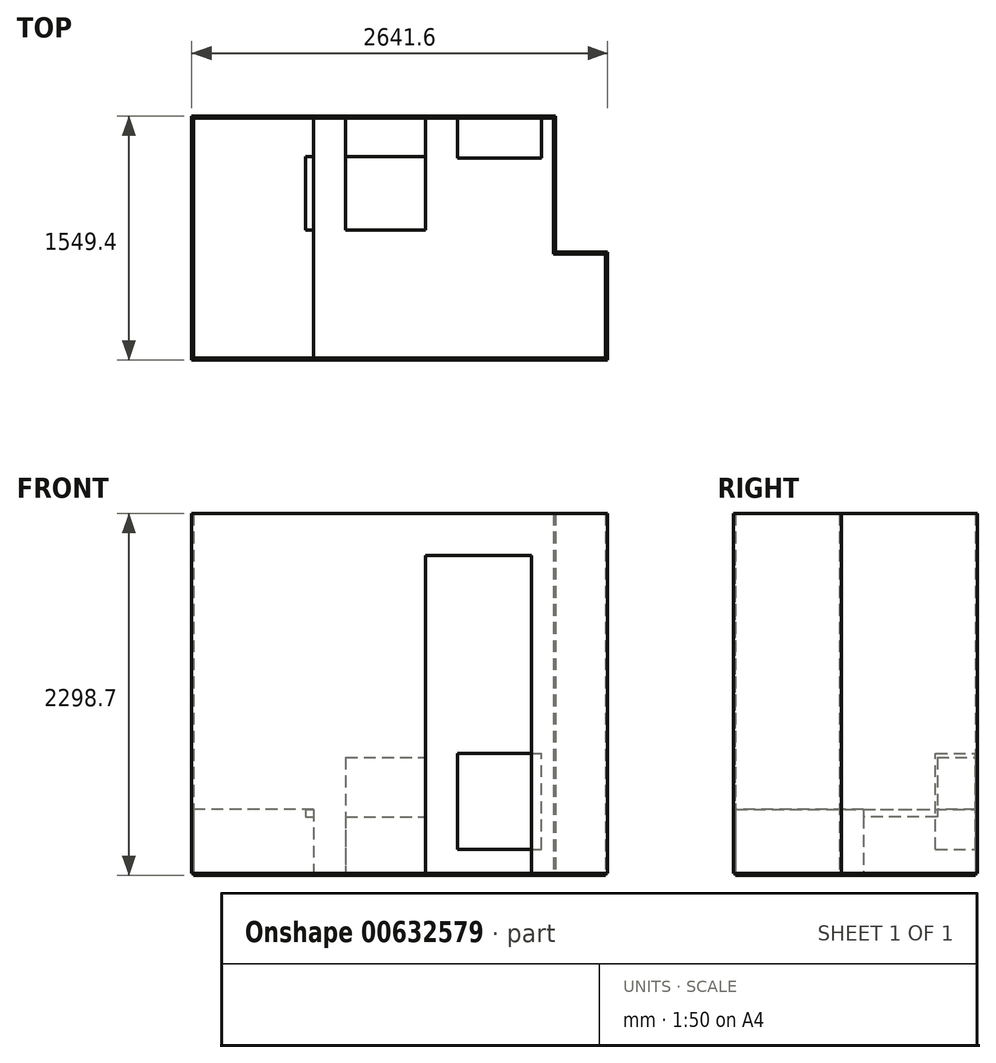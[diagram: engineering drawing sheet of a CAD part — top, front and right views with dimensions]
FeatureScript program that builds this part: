
annotation { "Feature Type Name" : "Feature", "Feature Type Description" : "" }
export const myFeature = defineFeature(function(context is Context, id is Id, definition is map)
    precondition{}
    {
        {
            var Q0;
            Q0=qCreatedBy(makeId("Top.planeOp"),FACE);
            var sketch = newSketch(context, id + "F0", { "sketchPlane" : qUnion([Q0])});
            skLineSegment(sketch, "E0.bottom", {"start": v(1143, -762) * mm, "end": v(-1143, -762) * mm});
            skLineSegment(sketch, "E0.top", {"start": v(1143, 762) * mm, "end": v(-1143, 762) * mm});
            skLineSegment(sketch, "E0.left", {"start": v(1143, -101.6) * mm, "end": v(1143, 762) * mm});
            skLineSegment(sketch, "E0.right", {"start": v(-1143, -762) * mm, "end": v(-1143, 762) * mm});
            skPoint(sketch, "E0.middle", {"position": v(0, 0) * mm});
            skLineSegment(sketch, "E1.bottom", {"start": v(1143, -762) * mm, "end": v(1473.2, -762) * mm});
            skLineSegment(sketch, "E1.top", {"start": v(1143, -101.6) * mm, "end": v(1473.2, -101.6) * mm});
            skLineSegment(sketch, "E1.right", {"start": v(1473.2, -762) * mm, "end": v(1473.2, -101.6) * mm});
            skSolve(sketch);
        }
        {
            var Q0;
            Q0=makeQuery(id+"F0.imprint","IMPRINT",FACE,{"disambiguationData":[TD([[makeQuery(id+"F0.imprint","IMPRINT",EDGE,{"derivedFrom":sQuery(id+"F0.wireOp",EDGE,"E0.bottom")}),-1.0]])]});
            extrude(context, id + "F1", {"entities" : qUnion([Q0]), "oppositeDirection" : true, "depth" : 12.7 * mm, "offsetDistance" : 25.4 * mm});
        }
        {
            var Q0;
            Q0=makeQuery(id+"F1.opExtrude","CAP_FACE",FACE,{"disambiguationData":[OSD([sQuery(id+"F0.wireOp",EDGE,"E0.bottom"),sQuery(id+"F0.wireOp",EDGE,"E0.top"),sQuery(id+"F0.wireOp",EDGE,"E0.left"),sQuery(id+"F0.wireOp",EDGE,"E0.right"),sQuery(id+"F0.wireOp",EDGE,"E1.bottom"),sQuery(id+"F0.wireOp",EDGE,"E1.top"),sQuery(id+"F0.wireOp",EDGE,"E1.right")])],"isStart":true});
            var sketch = newSketch(context, id + "F2", { "sketchPlane" : qUnion([Q0])});
            skLineSegment(sketch, "E2.0", {"start": v(1485.9, -774.7) * mm, "end": v(1485.9, -88.9) * mm});
            skLineSegment(sketch, "E2.1", {"start": v(1155.7, -88.9) * mm, "end": v(1155.7, 774.7) * mm});
            skLineSegment(sketch, "E2.2", {"start": v(1155.7, 774.7) * mm, "end": v(-1155.7, 774.7) * mm});
            skLineSegment(sketch, "E2.3", {"start": v(1485.9, -88.9) * mm, "end": v(1155.7, -88.9) * mm});
            skLineSegment(sketch, "E2.4", {"start": v(-1155.7, 774.7) * mm, "end": v(-1155.7, -774.7) * mm});
            skLineSegment(sketch, "E2.5", {"start": v(-1155.7, -774.7) * mm, "end": v(1485.9, -774.7) * mm});
            skSolve(sketch);
        }
        {
            var Q0;
            Q0=makeQuery(id+"F2.imprint","IMPRINT",FACE,{"disambiguationData":[TD([[makeQuery(id+"F2.imprint","IMPRINT",EDGE,{"derivedFrom":sQuery(id+"F2.wireOp",EDGE,"E2.0")}),1.0]])]});
            extrude(context, id + "F3", {"entities" : qUnion([Q0]), "depth" : 2286 * mm, "offsetDistance" : 25.4 * mm});
        }
        {
            var Q0;
            Q0=makeQuery(id+"F3.opExtrude","SWEPT_FACE",FACE,{"disambiguationData":[OSD([sQuery(id+"F2.wireOp",EDGE,"E2.5")])]});
            var sketch = newSketch(context, id + "F4", { "sketchPlane" : qUnion([Q0])});
            skLineSegment(sketch, "E3.bottom", {"start": v(330.2, 0) * mm, "end": v(1003.3, 0) * mm});
            skLineSegment(sketch, "E3.left", {"start": v(330.2, 0) * mm, "end": v(330.2, 2019.3) * mm});
            skLineSegment(sketch, "E3.right", {"start": v(1003.3, 0) * mm, "end": v(1003.3, 2019.3) * mm});
            skLineSegment(sketch, "E4", {"start": v(330.2, 2019.3) * mm, "end": v(1003.3, 2019.3) * mm});
            skPoint(sketch, "E3.top.end.orphan", {"position": v(1003.3, 2286) * mm});
            skPoint(sketch, "E3.top.start.orphan", {"position": v(330.2, 2286) * mm});
            skSolve(sketch);
        }
        {
            var Q0;
            Q0 = qSketchRegion(id + "F4", true);
            extrude(context, id + "F5", {"entities" : qUnion([Q0]), "operationType" : NewBodyOperationType.REMOVE, "oppositeDirection" : true, "depth" : 25.4 * mm, "offsetDistance" : 25.4 * mm});
        }
        {
            var Q0;
            Q0=makeQuery(id+"F1.opExtrude","CAP_FACE",FACE,{"disambiguationData":[OSD([sQuery(id+"F0.wireOp",EDGE,"E0.bottom"),sQuery(id+"F0.wireOp",EDGE,"E0.top"),sQuery(id+"F0.wireOp",EDGE,"E0.left"),sQuery(id+"F0.wireOp",EDGE,"E0.right"),sQuery(id+"F0.wireOp",EDGE,"E1.bottom"),sQuery(id+"F0.wireOp",EDGE,"E1.top"),sQuery(id+"F0.wireOp",EDGE,"E1.right")])],"isStart":true});
            var sketch = newSketch(context, id + "F6", { "sketchPlane" : qUnion([Q0])});
            skLineSegment(sketch, "E5.bottom", {"start": v(-1143, 762) * mm, "end": v(-381, 762) * mm});
            skLineSegment(sketch, "E5.top", {"start": v(-1143, -762) * mm, "end": v(-381, -762) * mm});
            skLineSegment(sketch, "E5.left", {"start": v(-1143, 762) * mm, "end": v(-1143, -762) * mm});
            skLineSegment(sketch, "E5.right", {"start": v(-381, 762) * mm, "end": v(-381, -762) * mm});
            skSolve(sketch);
        }
        {
            var Q0;
            Q0=makeQuery(id+"F3.opExtrude","SWEPT_FACE",FACE,{"disambiguationData":[OSD([sQuery(id+"F0.wireOp",EDGE,"E0.top")])]});
            var sketch = newSketch(context, id + "F7", { "sketchPlane" : qUnion([Q0])});
            skSolve(sketch);
        }
        {
            var Q0;
            Q0=makeQuery(id+"F6.imprint","IMPRINT",FACE,{"disambiguationData":[TD([[makeQuery(id+"F6.imprint","IMPRINT",EDGE,{"derivedFrom":sQuery(id+"F6.wireOp",EDGE,"E5.bottom")}),1.0]])]});
            extrude(context, id + "F8", {"entities" : qUnion([Q0]), "depth" : 406.4 * mm, "offsetDistance" : 25.4 * mm});
        }
        {
            var Q0;
            {var subQ0=sQuery(id+"F0.wireOp",EDGE,"E0.top");Q0=makeQuery(id+"F7.imprint","IMPRINT",FACE,{"disambiguationData":[TD([[makeQuery(id+"F7.imprint","IMPRINT",EDGE,{"derivedFrom":makeQuery(id+"F3.opExtrude","CAP_EDGE",EDGE,{"disambiguationData":[OSD([subQ0])],"isStart":true})}),-1.0]])]});}
            var sketch = newSketch(context, id + "F9", { "sketchPlane" : qUnion([Q0])});
            skLineSegment(sketch, "E6.0", {"start": v(-381, 406.4) * mm, "end": v(-381, 0) * mm});
            skLineSegment(sketch, "E7.0", {"start": v(1143, 2286) * mm, "end": v(1143, 0) * mm});
            skLineSegment(sketch, "E8", {"start": v(-177.8, 736.6) * mm, "end": v(-177.8, 0) * mm});
            skLineSegment(sketch, "E9", {"start": v(330.2, 736.6) * mm, "end": v(330.2, 0) * mm});
            skLineSegment(sketch, "E10.trimOffspring", {"start": v(330.2, 736.6) * mm, "end": v(-177.8, 736.6) * mm});
            skPoint(sketch, "E11.start.orphan", {"position": v(-381, 736.6) * mm});
            skPoint(sketch, "E12.orphan", {"position": v(533.4, 0) * mm});
            skPoint(sketch, "E13.start.orphan", {"position": v(533.4, 736.6) * mm});
            skPoint(sketch, "E14.right.end.orphan", {"position": v(1066.8, 909.6) * mm});
            skPoint(sketch, "E15.end.orphan", {"position": v(1066.8, 0) * mm});
            skPoint(sketch, "E15.start.orphan", {"position": v(1066.8, 736.6) * mm});
            skLineSegment(sketch, "E16.bottom", {"start": v(533.4, 152.4) * mm, "end": v(1066.8, 152.4) * mm});
            skLineSegment(sketch, "E16.top", {"start": v(533.4, 762) * mm, "end": v(1066.8, 762) * mm});
            skLineSegment(sketch, "E16.left", {"start": v(533.4, 152.4) * mm, "end": v(533.4, 762) * mm});
            skLineSegment(sketch, "E16.right", {"start": v(1066.8, 152.4) * mm, "end": v(1066.8, 762) * mm});
            skSolve(sketch);
        }
        {
            var Q0;
            {var subQ0=sQuery(id+"F9.wireOp",EDGE,"E8");Q0=makeQuery(id+"F9.imprint","IMPRINT",FACE,{"disambiguationData":[TD([[makeQuery(id+"F9.imprint","IMPRINT",EDGE,{"derivedFrom":subQ0}),1.0]])]});}
            extrude(context, id + "F10", {"entities" : qUnion([Q0]), "depth" : 711.2 * mm, "offsetDistance" : 25.4 * mm});
        }
        {
            var Q0;
            Q0=makeQuery(id+"F9.imprint","IMPRINT",FACE,{"disambiguationData":[TD([[makeQuery(id+"F9.imprint","IMPRINT",EDGE,{"derivedFrom":sQuery(id+"F9.wireOp",EDGE,"E16.bottom")}),1.0]])]});
            extrude(context, id + "F11", {"entities" : qUnion([Q0]), "operationType" : NewBodyOperationType.ADD, "depth" : 254 * mm, "offsetDistance" : 25.4 * mm});
        }
        {
            var Q0;
            Q0=makeQuery(id+"F10.opExtrude","SWEPT_FACE",FACE,{"disambiguationData":[OSD([sQuery(id+"F9.wireOp",EDGE,"E9")])]});
            var sketch = newSketch(context, id + "F12", { "sketchPlane" : qUnion([Q0])});
            skLineSegment(sketch, "E17", {"start": v(517.86, 736.6) * mm, "end": v(517.86, 359.56) * mm});
            skLineSegment(sketch, "E18", {"start": v(517.86, 359.56) * mm, "end": v(50.8, 359.56) * mm});
            skLineSegment(sketch, "E19", {"start": v(50.8, 359.56) * mm, "end": v(50.8, 736.6) * mm});
            skLineSegment(sketch, "E20", {"start": v(50.8, 736.6) * mm, "end": v(517.86, 736.6) * mm});
            skSolve(sketch);
        }
        {
            var Q0;
            Q0 = qSketchRegion(id + "F12", true);
            extrude(context, id + "F13", {"entities" : qUnion([Q0]), "operationType" : NewBodyOperationType.REMOVE, "oppositeDirection" : true, "depth" : 762 * mm, "offsetDistance" : 25.4 * mm});
        }
    });
